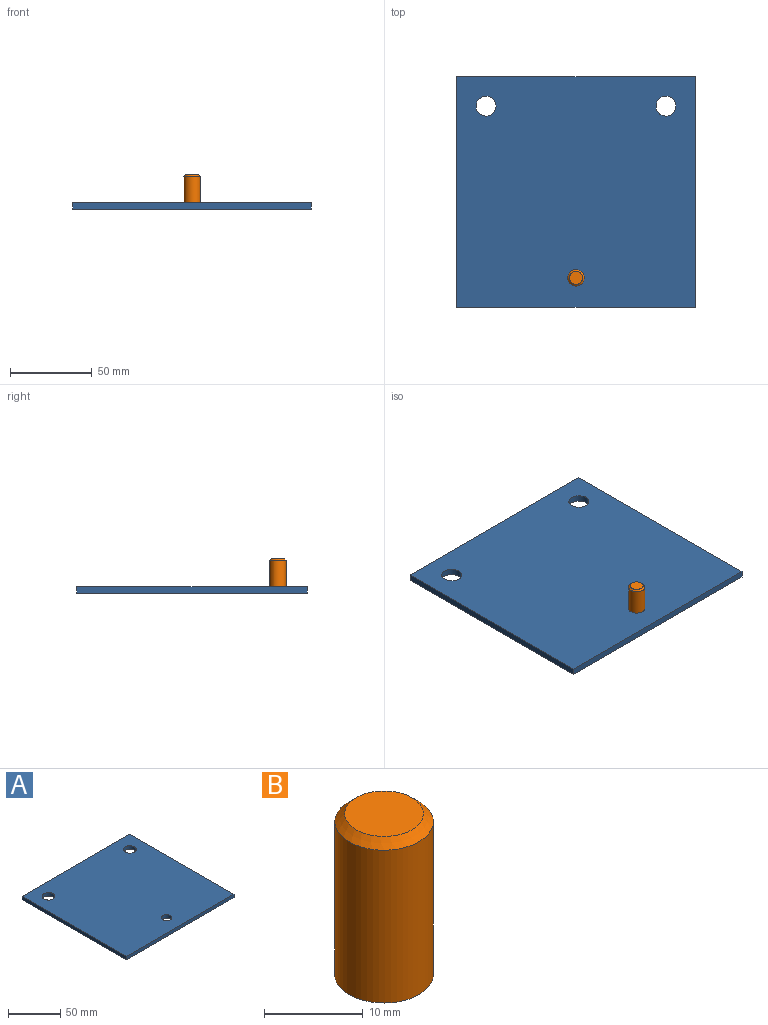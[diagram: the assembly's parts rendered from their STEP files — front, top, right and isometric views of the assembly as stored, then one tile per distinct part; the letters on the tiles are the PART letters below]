
ASSEMBLY  parts=2 mates=1
PART A: 9 faces, bbox 146x141x4 mm
  f0: plane 141x4mm, normal (1,0,0), area 564mm2, adj f1,f5,f7,f8
  f1: plane 146x4mm, normal (0,1,0), area 584mm2, adj f0,f2,f7,f8
  f2: plane 141x4mm, normal (-1,0,0), area 564mm2, adj f1,f5,f7,f8
  f3: cylinder r=5mm len=10mm, axis (0,0,-1), area 125.7mm2, adj f7,f8
  f4: cylinder r=6.1mm len=12.2mm, axis (0,0,-1), area 153.3mm2, adj f7,f8
  f5: plane 146x4mm, normal (0,-1,0), area 584mm2, adj f0,f2,f7,f8
  f6: cylinder r=6.1mm len=12.2mm, axis (0,0,-1), area 153.3mm2, adj f7,f8
  f7: plane 146x141mm, normal (0,0,1), area 20273.7mm2, adj f0,f1,f2,f3,f4,f5,f6
  f8: plane 146x141mm, normal (0,0,-1), area 20273.7mm2, adj f0,f1,f2,f3,f4,f5,f6
PART B: 4 faces, bbox 10x10x20 mm
  f0: cylinder r=5mm len=19mm, axis (0,0,-1), area 596.9mm2, adj f2,f3
  f1: plane 8x8mm, normal (0,0,1), area 50.3mm2, adj f3
  f2: plane 10x10mm, normal (0,0,-1), area 78.5mm2, adj f0
  f3: cone r=4mm half-angle=45deg, axis (0,0,-1), area 40mm2, adj f0,f1
PLACE A t=(64.85,24.05,-22.09)mm
PLACE B t=(64.85,-28.45,-21.09)mm
MATE fastened B.f0 <-> A.f3  axis (0,0,-1) through (64.85,-28.45,-21.09)mm
